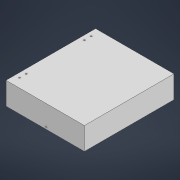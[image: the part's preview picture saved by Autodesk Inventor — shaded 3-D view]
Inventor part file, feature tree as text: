
AUTODESK INVENTOR PART (.ipt)
format: ipt  version: 2021 (Build 250183000, 183)  size: 269,824 bytes
history: native  units: mm
features: extrude x5, sketch x5, other x1
ambient origin geometry x8: Origin, YZ Plane, XZ Plane, XY Plane, X Axis, Y Axis, Z Axis, Center Point
bodies: Volumenkörper1 (feature_tree)
feature tree (11):
  other  "Ebene3_hinten"
  extrude  "Extrusion1"  Depth=200.0mm
  extrude  "Extrusion2"  Depth=2.0mm
  extrude  "Extrusion3"  Depth=2.0mm
  extrude  "Extrusion4"  Depth=48.0mm
  extrude  "Extrusion5"  Depth=50.0mm
  sketch  "Skizze1"  dims[d0=175.0mm d1=200.0mm]
  sketch  "Skizze2"  dims[d2=2.0mm d3=0.0mm d4=2.0mm]
  sketch  "Skizze3"  dims[d5=2.0mm d6=2.0mm]
  sketch  "Skizze4"  dims[d7=48.0mm d8=0.0mm d9=3.2mm]
  sketch  "Skizze5"  dims[d10=3.2mm d11=3.2mm d12=3.2mm d13=10.0mm d14=10.0mm d15=15.0mm d16=20.0mm d17=10.0mm d18=10.0mm d19=20.0mm d20=15.0mm d21=2.0mm d22=0.0mm d23=3.2mm d24=85.0mm d25=5.0mm d26=50.0mm d27=0.0mm d28=3.2mm d29=5.0mm d30=85.0mm d31=50.0mm d32=0.0mm]
